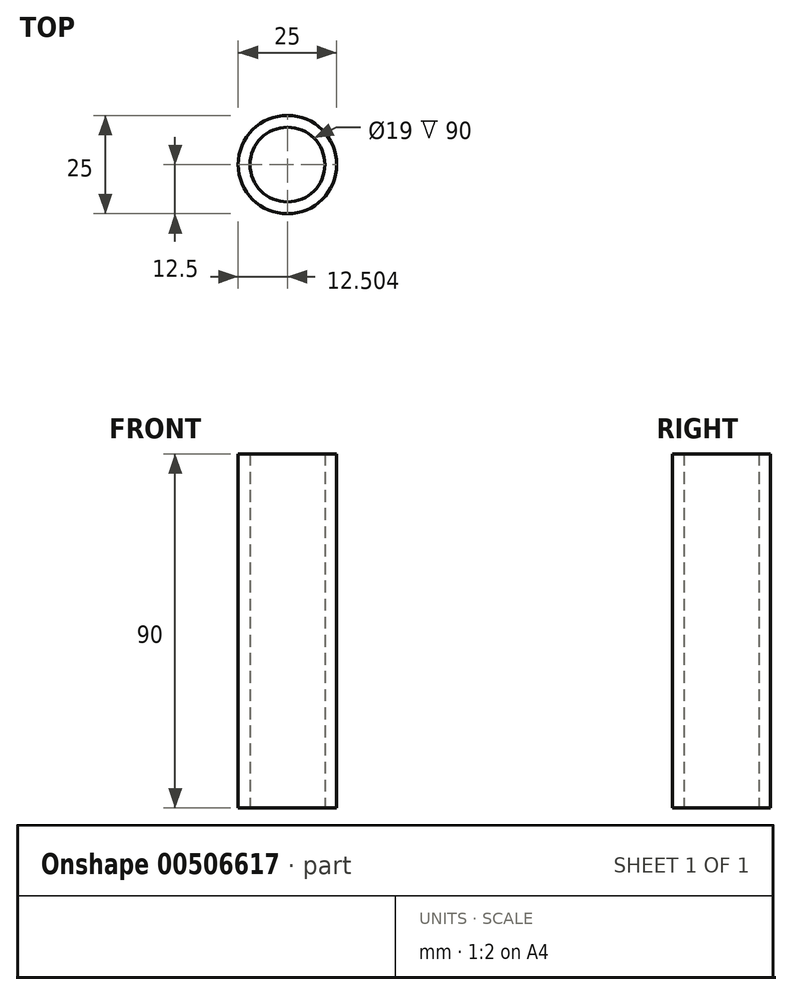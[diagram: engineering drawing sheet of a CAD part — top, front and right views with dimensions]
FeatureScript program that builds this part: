
annotation { "Feature Type Name" : "Feature", "Feature Type Description" : "" }
export const myFeature = defineFeature(function(context is Context, id is Id, definition is map)
    precondition{}
    {
        {
            var Q0;
            Q0=qCreatedBy(makeId("Top.planeOp"),FACE);
            var sketch = newSketch(context, id + "F0", { "sketchPlane" : qUnion([Q0])});
            skCircle(sketch, "E0", {"center": v(4.87, 9.95) * mm, "radius": 12.5 * mm});
            skCircle(sketch, "E1", {"center": v(4.87, 9.95) * mm, "radius": 9.5 * mm});
            skSolve(sketch);
        }
        {
            var Q0;
            Q0 = qSketchRegion(id + "F0", true);
            extrude(context, id + "F1", {"entities" : qUnion([Q0]), "depth" : 90 * mm});
        }
    });
